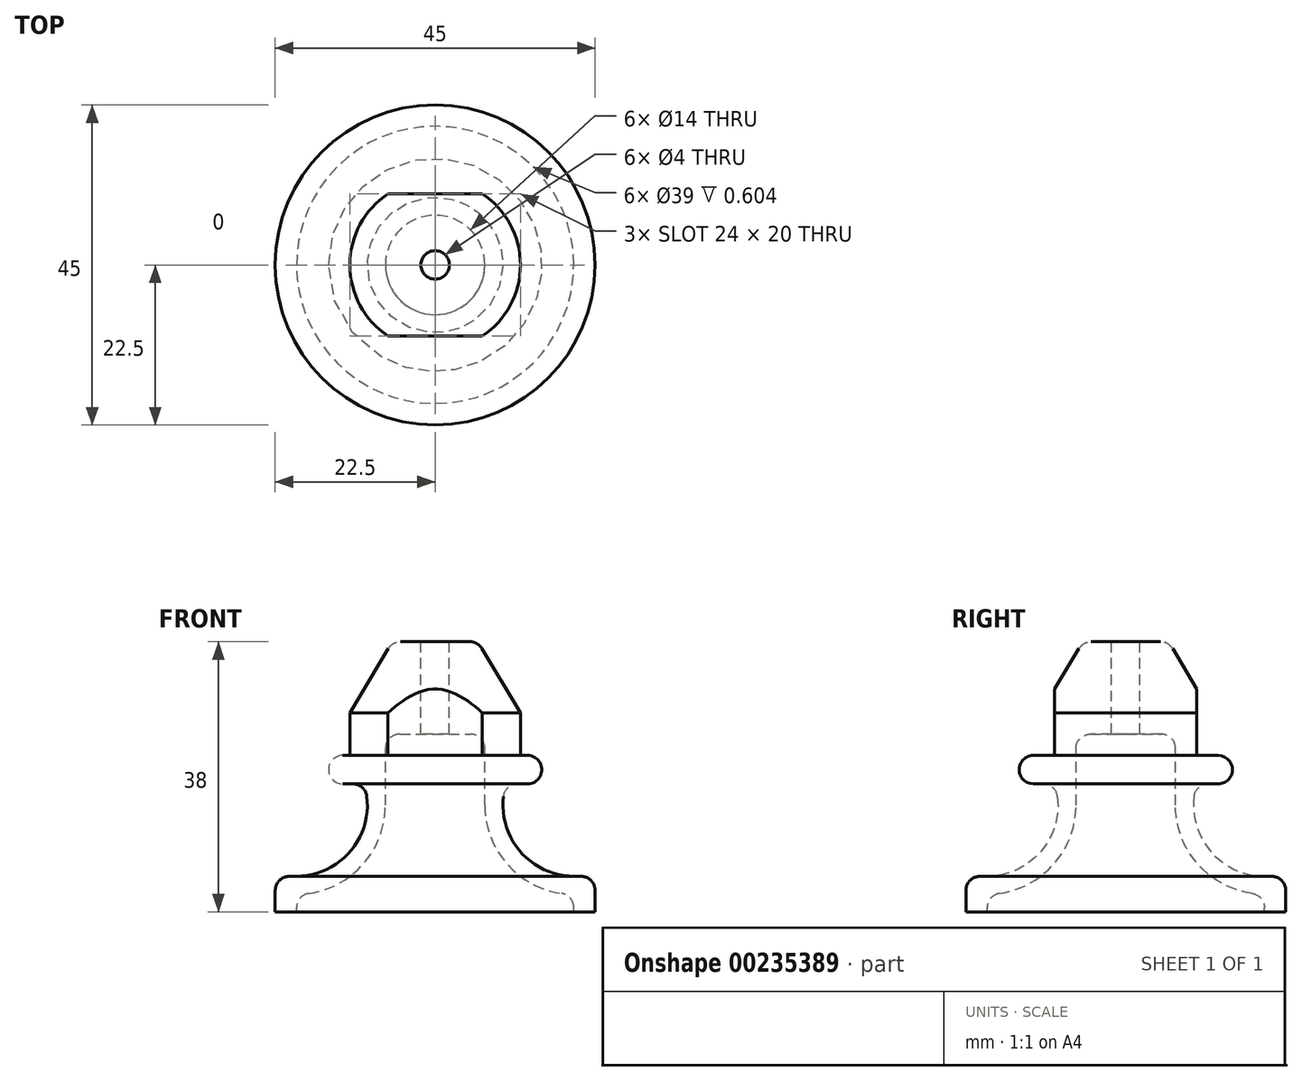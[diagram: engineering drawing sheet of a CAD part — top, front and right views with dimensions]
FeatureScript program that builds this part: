
annotation { "Feature Type Name" : "Feature", "Feature Type Description" : "" }
export const myFeature = defineFeature(function(context is Context, id is Id, definition is map)
    precondition{}
    {
        {
            var Q0;
            Q0=qCreatedBy(makeId("Front.planeOp"),FACE);
            var sketch = newSketch(context, id + "F0", { "sketchPlane" : qUnion([Q0])});
            skLineSegment(sketch, "E0", {"start": v(-2, 35.54) * mm, "end": v(-6, 35.54) * mm});
            skLineSegment(sketch, "E1", {"start": v(-6, 35.54) * mm, "end": v(-12, 25.54) * mm});
            skLineSegment(sketch, "E2", {"start": v(-12, 25.54) * mm, "end": v(-12, 19.54) * mm});
            skLineSegment(sketch, "E3", {"start": v(-12, 19.54) * mm, "end": v(-15, 19.54) * mm});
            skLineSegment(sketch, "E4", {"start": v(-15, 19.54) * mm, "end": v(-15, 15.54) * mm});
            skLineSegment(sketch, "E5", {"start": v(-15, 15.54) * mm, "end": v(-10, 15.54) * mm});
            skArc(sketch, "E6", {"start": v(-19.54, 2.54) * mm, "mid": v(-11.48, 6.62) * mm, "end": v(-10, 15.54) * mm});
            skLineSegment(sketch, "E7", {"start": v(-19.54, 2.54) * mm, "end": v(-22.5, 2.54) * mm});
            skLineSegment(sketch, "E8", {"start": v(-22.5, 2.54) * mm, "end": v(-22.5, -2.46) * mm});
            skArc(sketch, "E9.0", {"start": v(-19.5, 0) * mm, "mid": v(-10.66, 3.69) * mm, "end": v(-7, 12.54) * mm});
            skLineSegment(sketch, "E10", {"start": v(-7, 12.54) * mm, "end": v(-7, 22.54) * mm});
            skLineSegment(sketch, "E11", {"start": v(-7, 22.54) * mm, "end": v(-2, 22.54) * mm});
            skLineSegment(sketch, "E12", {"start": v(-2, 22.54) * mm, "end": v(-2, 35.54) * mm});
            skLineSegment(sketch, "E13", {"start": v(-19.5, 0) * mm, "end": v(-19.5, -2.46) * mm});
            skLineSegment(sketch, "E14", {"start": v(-19.5, -2.46) * mm, "end": v(-22.5, -2.46) * mm});
            skLineSegment(sketch, "E15", {"start": v(0, 55.21) * mm, "end": v(0, -26.74) * mm, "construction": true});
            skSolve(sketch);
        }
        {
            var Q0;
            Q0=makeQuery(id+"F0.imprint","IMPRINT",FACE,{"disambiguationData":[TD([[makeQuery(id+"F0.imprint","IMPRINT",EDGE,{"derivedFrom":sQuery(id+"F0.wireOp",EDGE,"E0")}),1.0]])]});
            var Q1;
            Q1=sQuery(id+"F0.wireOp",EDGE,"E15");
            revolve(context, id + "F1", {"entities" : qUnion([Q0]), "axis" : qUnion([Q1]), "revolveType" : RevolveType.FULL});
        }
        {
            var Q0;
            Q0=makeQuery(id+"F1.opRevolve","SWEPT_EDGE",EDGE,{"disambiguationData":[OSD([sQuery(id+"F0.wireOp",EDGE,"E7"),sQuery(id+"F0.wireOp",EDGE,"E8")])]});
            var Q1;
            Q1=makeQuery(id+"F1.opRevolve","SWEPT_EDGE",EDGE,{"disambiguationData":[OSD([sQuery(id+"F0.wireOp",EDGE,"E4"),sQuery(id+"F0.wireOp",EDGE,"E5")])]});
            var Q2;
            Q2=makeQuery(id+"F1.opRevolve","SWEPT_EDGE",EDGE,{"disambiguationData":[OSD([sQuery(id+"F0.wireOp",EDGE,"E3"),sQuery(id+"F0.wireOp",EDGE,"E4")])]});
            var Q3;
            Q3=makeQuery(id+"F1.opRevolve","SWEPT_EDGE",EDGE,{"disambiguationData":[OSD([sQuery(id+"F0.wireOp",EDGE,"E0"),sQuery(id+"F0.wireOp",EDGE,"E1")])]});
            var Q4;
            Q4=makeQuery(id+"F1.opRevolve","SWEPT_FACE",FACE,{"disambiguationData":[OSD([sQuery(id+"F0.wireOp",EDGE,"E9.0")])]});
            var Q5;
            Q5=makeQuery(id+"F1.opRevolve","SWEPT_EDGE",EDGE,{"disambiguationData":[OSD([sQuery(id+"F0.wireOp",EDGE,"E10"),sQuery(id+"F0.wireOp",EDGE,"E11")])]});
            var Q6;
            Q6=makeQuery(id+"F1.opRevolve","SWEPT_EDGE",EDGE,{"disambiguationData":[OSD([sQuery(id+"F0.wireOp",EDGE,"E5"),sQuery(id+"F0.wireOp",EDGE,"E6")])]});
            fillet(context, id + "F2", {"entities" : qUnion([Q0, Q1, Q2, Q3, Q4, Q5, Q6]), "radius" : 2 * mm, "tangentPropagation" : true, "allowEdgeOverflow" : false});
        }
        {
            var Q0;
            Q0=makeQuery(id+"F1.opRevolve","SWEPT_FACE",FACE,{"disambiguationData":[OSD([sQuery(id+"F0.wireOp",EDGE,"E0")])]});
            var sketch = newSketch(context, id + "F3", { "sketchPlane" : qUnion([Q0])});
            skCircle(sketch, "E16.0.0", {"center": v(0, 0) * mm, "radius": 4.87 * mm});
            skLineSegment(sketch, "E17.bottom", {"start": v(8.3, -10) * mm, "end": v(-8.3, -10) * mm});
            skLineSegment(sketch, "E17.top", {"start": v(8.3, 10) * mm, "end": v(-8.3, 10) * mm});
            skLineSegment(sketch, "E17.left", {"start": v(8.3, -10) * mm, "end": v(8.3, 10) * mm});
            skLineSegment(sketch, "E17.right", {"start": v(-8.3, -10) * mm, "end": v(-8.3, 10) * mm});
            skCircle(sketch, "E18.0", {"center": v(0, 0) * mm, "radius": 13 * mm});
            skSolve(sketch);
        }
        {
            var Q0;
            {var subQ0=sQuery(id+"F3.wireOp",EDGE,"E17.top");Q0=makeQuery(id+"F3.imprint","IMPRINT",FACE,{"disambiguationData":[TD([[makeQuery(id+"F3.imprint","IMPRINT",EDGE,{"derivedFrom":subQ0}),-1.0]])]});}
            var Q1;
            {var subQ0=sQuery(id+"F3.wireOp",EDGE,"E17.bottom");Q1=makeQuery(id+"F3.imprint","IMPRINT",FACE,{"disambiguationData":[TD([[makeQuery(id+"F3.imprint","IMPRINT",EDGE,{"derivedFrom":subQ0}),1.0]])]});}
            var Q2;
            Q2=makeQuery(id+"F1.opRevolve","SWEPT_FACE",FACE,{"disambiguationData":[OSD([sQuery(id+"F0.wireOp",EDGE,"E3")])]});
            extrude(context, id + "F4", {"entities" : qUnion([Q0, Q1]), "operationType" : NewBodyOperationType.REMOVE, "endBound" : BoundingType.UP_TO_SURFACE, "oppositeDirection" : true, "endBoundEntityFace" : qUnion([Q2]), "depth" : 25 * mm});
        }
    });
